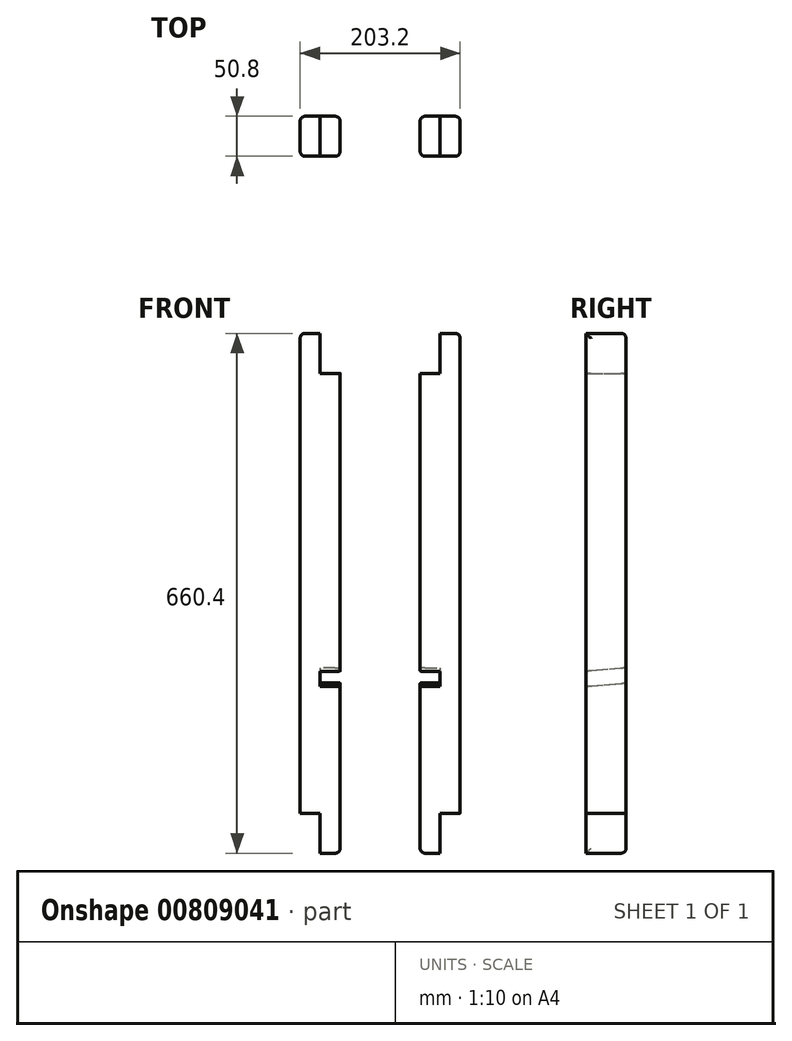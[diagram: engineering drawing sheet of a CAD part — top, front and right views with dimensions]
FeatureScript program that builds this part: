
annotation { "Feature Type Name" : "Feature", "Feature Type Description" : "" }
export const myFeature = defineFeature(function(context is Context, id is Id, definition is map)
    precondition{}
    {
        {
            var Q0;
            Q0=qCreatedBy(makeId("Top.planeOp"),FACE);
            var sketch = newSketch(context, id + "F0", { "sketchPlane" : qUnion([Q0])});
            skLineSegment(sketch, "E0.bottom", {"start": v(0, 0) * mm, "end": v(25.4, 0) * mm});
            skLineSegment(sketch, "E0.top", {"start": v(0, 50.8) * mm, "end": v(25.4, 50.8) * mm});
            skLineSegment(sketch, "E0.left", {"start": v(0, 0) * mm, "end": v(0, 50.8) * mm});
            skLineSegment(sketch, "E0.right", {"start": v(25.4, 0) * mm, "end": v(25.4, 50.8) * mm});
            skLineSegment(sketch, "E1.bottom", {"start": v(0, 0) * mm, "end": v(-25.4, 0) * mm});
            skLineSegment(sketch, "E1.top", {"start": v(0, 50.8) * mm, "end": v(-25.4, 50.8) * mm});
            skLineSegment(sketch, "E1.right", {"start": v(-25.4, 0) * mm, "end": v(-25.4, 50.8) * mm});
            skSolve(sketch);
        }
        {
            var Q0;
            Q0=makeQuery(id+"F0.imprint","IMPRINT",FACE,{"disambiguationData":[TD([[makeQuery(id+"F0.imprint","IMPRINT",EDGE,{"derivedFrom":sQuery(id+"F0.wireOp",EDGE,"E0.bottom")}),1.0]])]});
            extrude(context, id + "F1", {"entities" : qUnion([Q0]), "depth" : 609.6 * mm, "offsetDistance" : 25.4 * mm});
        }
        {
            var Q0;
            Q0=makeQuery(id+"F0.imprint","IMPRINT",FACE,{"disambiguationData":[TD([[makeQuery(id+"F0.imprint","IMPRINT",EDGE,{"derivedFrom":sQuery(id+"F0.wireOp",EDGE,"E1.bottom")}),-1.0]])]});
            extrude(context, id + "F2", {"entities" : qUnion([Q0]), "operationType" : NewBodyOperationType.ADD, "oppositeDirection" : true, "depth" : 50.8 * mm, "offsetDistance" : 25.4 * mm, "hasSecondDirection" : true, "secondDirectionOppositeDirection" : false, "secondDirectionDepth" : 558.8 * mm});
        }
        {
            var Q0;
            Q0=qCreatedBy(makeId("Right.planeOp"),FACE);
            var sketch = newSketch(context, id + "F3", { "sketchPlane" : qUnion([Q0])});
            skLineSegment(sketch, "E2", {"start": v(0, 161.16) * mm, "end": v(50.8, 165.6) * mm});
            skLineSegment(sketch, "E3", {"start": v(50.8, 165.6) * mm, "end": v(50.8, 184.66) * mm});
            skLineSegment(sketch, "E4", {"start": v(50.8, 184.66) * mm, "end": v(0, 180.21) * mm});
            skLineSegment(sketch, "E5", {"start": v(0, 180.21) * mm, "end": v(0, 161.16) * mm});
            skSolve(sketch);
        }
        {
            var Q0;
            Q0=qSketchRegion(id+"F3",true);
            extrude(context, id + "F4", {"entities" : qUnion([Q0]), "operationType" : NewBodyOperationType.REMOVE, "oppositeDirection" : true, "depth" : 25.4 * mm, "offsetDistance" : 25.4 * mm});
        }
        {
            var Q0;
            Q0=makeQuery(id+"F2.opExtrude","SWEPT_EDGE",EDGE,{"disambiguationData":[OSD([sQuery(id+"F0.wireOp",EDGE,"E1.top"),sQuery(id+"F0.wireOp",EDGE,"E1.right")])]});
            var Q1;
            Q1=makeQuery(id+"F2.opExtrude","CAP_EDGE",EDGE,{"disambiguationData":[OSD([sQuery(id+"F0.wireOp",EDGE,"E1.top")])],"isStart":false});
            var Q2;
            Q2=makeQuery(id+"F2.opExtrude","CAP_EDGE",EDGE,{"disambiguationData":[OSD([sQuery(id+"F0.wireOp",EDGE,"E1.right")])],"isStart":false});
            var Q3;
            Q3=makeQuery(id+"F2.opExtrude","SWEPT_EDGE",EDGE,{"disambiguationData":[OSD([sQuery(id+"F0.wireOp",EDGE,"E1.bottom"),sQuery(id+"F0.wireOp",EDGE,"E1.right")])]});
            var Q4;
            {var subQ0=sQuery(id+"F0.wireOp",EDGE,"E0.right");var subQ1=sQuery(id+"F0.wireOp",EDGE,"E0.bottom");Q4=makeQuery(id+"F4.boolean.opBoolean","SPLIT",EDGE,{"disambiguationData":[TD([makeQuery(id+"F4.opExtrude","SWEPT_FACE",FACE,{"disambiguationData":[OSD([sQuery(id+"F3.wireOp",EDGE,"E2")])]})])],"derivedFrom":makeQuery(id+"F1.opExtrude","SWEPT_EDGE",EDGE,{"disambiguationData":[OSD([subQ1,subQ0])]})});}
            var Q5;
            {var subQ0=sQuery(id+"F0.wireOp",EDGE,"E0.right");var subQ1=sQuery(id+"F0.wireOp",EDGE,"E0.top");Q5=makeQuery(id+"F4.boolean.opBoolean","SPLIT",EDGE,{"disambiguationData":[TD([makeQuery(id+"F4.opExtrude","SWEPT_FACE",FACE,{"disambiguationData":[OSD([sQuery(id+"F3.wireOp",EDGE,"E2")])]})])],"derivedFrom":makeQuery(id+"F1.opExtrude","SWEPT_EDGE",EDGE,{"disambiguationData":[OSD([subQ1,subQ0])]})});}
            var Q6;
            {var subQ0=sQuery(id+"F0.wireOp",EDGE,"E0.right");var subQ1=sQuery(id+"F0.wireOp",EDGE,"E0.top");Q6=makeQuery(id+"F4.boolean.opBoolean","SPLIT",EDGE,{"disambiguationData":[TD([makeQuery(id+"F4.opExtrude","SWEPT_FACE",FACE,{"disambiguationData":[OSD([sQuery(id+"F3.wireOp",EDGE,"E4")])]})])],"derivedFrom":makeQuery(id+"F1.opExtrude","SWEPT_EDGE",EDGE,{"disambiguationData":[OSD([subQ1,subQ0])]})});}
            var Q7;
            {var subQ0=sQuery(id+"F0.wireOp",EDGE,"E0.right");var subQ1=sQuery(id+"F0.wireOp",EDGE,"E0.bottom");Q7=makeQuery(id+"F4.boolean.opBoolean","SPLIT",EDGE,{"disambiguationData":[TD([makeQuery(id+"F4.opExtrude","SWEPT_FACE",FACE,{"disambiguationData":[OSD([sQuery(id+"F3.wireOp",EDGE,"E4")])]})])],"derivedFrom":makeQuery(id+"F1.opExtrude","SWEPT_EDGE",EDGE,{"disambiguationData":[OSD([subQ1,subQ0])]})});}
            var Q8;
            Q8=makeQuery(id+"F1.opExtrude","CAP_EDGE",EDGE,{"disambiguationData":[OSD([sQuery(id+"F0.wireOp",EDGE,"E0.right")])],"isStart":false});
            var Q9;
            Q9=makeQuery(id+"F1.opExtrude","CAP_EDGE",EDGE,{"disambiguationData":[OSD([sQuery(id+"F0.wireOp",EDGE,"E0.top")])],"isStart":false});
            fillet(context, id + "F5", {"entities" : qUnion([Q0, Q1, Q2, Q3, Q4, Q5, Q6, Q7, Q8, Q9]), "radius" : 6.35 * mm, "tangentPropagation" : true, "allowEdgeOverflow" : false});
        }
        {
            var Q0;
            Q0=qCreatedBy(makeId("Right.planeOp"),FACE);
            cPlane(context, id + "F6", {"entities" : qUnion([Q0]), "cplaneType" : CPlaneType.OFFSET, "offset" : 76.2 * mm, "oppositeDirection" : true, "width" : 152.4 * mm, "height" : 152.4 * mm});
        }
        {
            var Q0;
            Q0=makeQuery(id+"F1.opExtrude","SWEPT_BODY",BODY,{"disambiguationData":[OSD([sQuery(id+"F0.wireOp",EDGE,"E0.bottom"),sQuery(id+"F0.wireOp",EDGE,"E0.top"),sQuery(id+"F0.wireOp",EDGE,"E0.right"),sQuery(id+"F0.wireOp",EDGE,"E0.left")])]});
            var Q1;
            Q1=qCreatedBy(id+"F6.planeOp",FACE);
            mirror(context, id + "F7", {"entities" : qUnion([Q0]), "mirrorPlane" : qUnion([Q1])});
        }
    });
